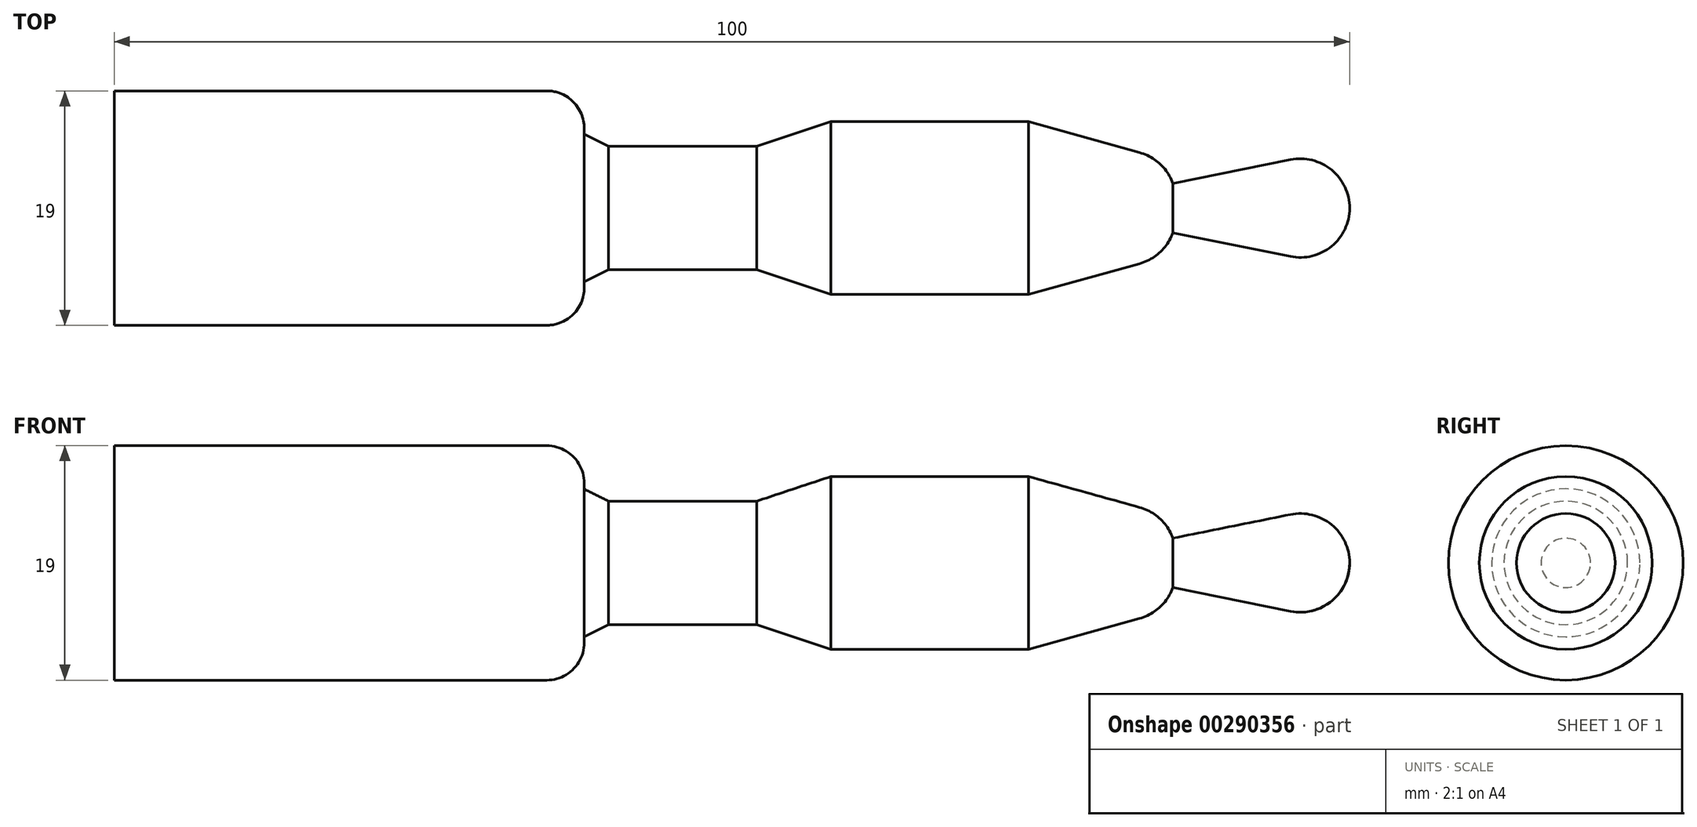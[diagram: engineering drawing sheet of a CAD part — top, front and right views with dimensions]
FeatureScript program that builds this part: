
annotation { "Feature Type Name" : "Feature", "Feature Type Description" : "" }
export const myFeature = defineFeature(function(context is Context, id is Id, definition is map)
    precondition{}
    {
        {
            var Q0;
            Q0=qCreatedBy(makeId("Front.planeOp"),FACE);
            var sketch = newSketch(context, id + "F0", { "sketchPlane" : qUnion([Q0])});
            skArc(sketch, "E0", {"start": v(0, 0) * mm, "mid": v(-1.47, 3.1) * mm, "end": v(-4.8, 3.92) * mm});
            skLineSegment(sketch, "E1", {"start": v(-4.8, 3.92) * mm, "end": v(-14.3, 2) * mm});
            skArc(sketch, "E2", {"start": v(-14.3, 2) * mm, "mid": v(-15.35, 3.58) * mm, "end": v(-17, 4.5) * mm});
            skLineSegment(sketch, "E3", {"start": v(-17, 4.5) * mm, "end": v(-26, 7) * mm});
            skLineSegment(sketch, "E4", {"start": v(-26, 7) * mm, "end": v(-42, 7) * mm});
            skLineSegment(sketch, "E5", {"start": v(-42, 7) * mm, "end": v(-48, 5) * mm});
            skLineSegment(sketch, "E6", {"start": v(-65, 9.5) * mm, "end": v(-100, 9.5) * mm});
            skLineSegment(sketch, "E7", {"start": v(-100, 9.5) * mm, "end": v(-100, 0) * mm});
            skLineSegment(sketch, "E8", {"start": v(-100, 0) * mm, "end": v(0, 0) * mm});
            skLineSegment(sketch, "E9", {"start": v(-48, 5) * mm, "end": v(-60, 5) * mm});
            skLineSegment(sketch, "E10", {"start": v(-60, 5) * mm, "end": v(-62, 6) * mm});
            skArc(sketch, "E11", {"start": v(-62, 6) * mm, "mid": v(-62.7, 8.44) * mm, "end": v(-65, 9.5) * mm});
            skSolve(sketch);
        }
        {
            var Q0;
            Q0 = qSketchRegion(id + "F0", true);
            var Q1;
            Q1=sQuery(id+"F0.wireOp",EDGE,"E8");
            revolve(context, id + "F1", {"entities" : qUnion([Q0]), "axis" : qUnion([Q1]), "revolveType" : RevolveType.FULL});
        }
    });
